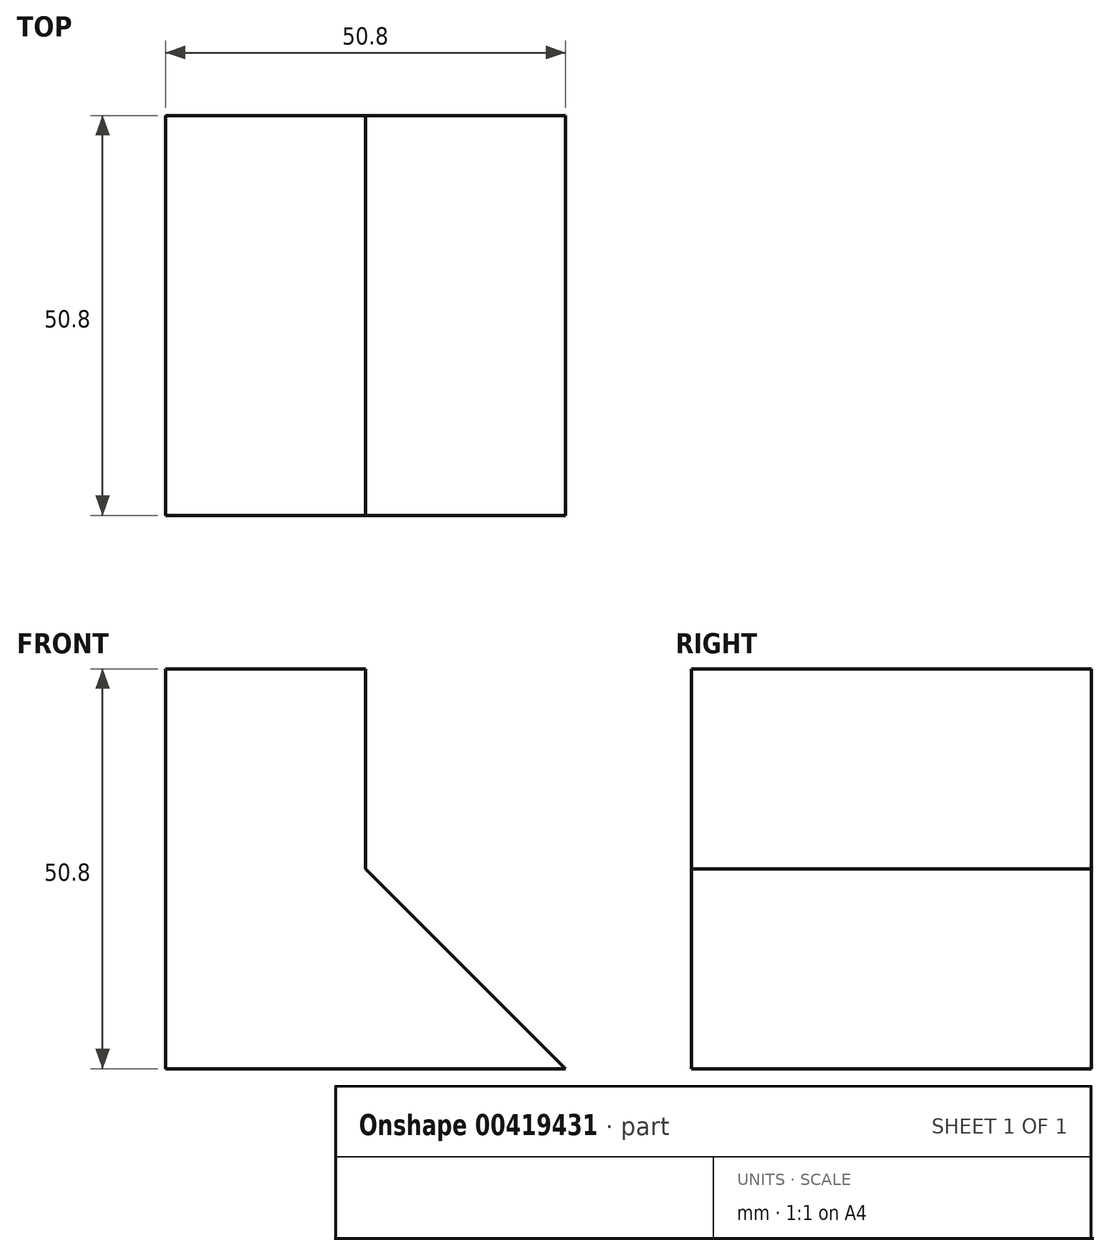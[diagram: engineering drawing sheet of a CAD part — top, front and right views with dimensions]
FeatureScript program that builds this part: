
annotation { "Feature Type Name" : "Feature", "Feature Type Description" : "" }
export const myFeature = defineFeature(function(context is Context, id is Id, definition is map)
    precondition{}
    {
        {
            var Q0;
            Q0=qCreatedBy(makeId("Front.planeOp"),FACE);
            var sketch = newSketch(context, id + "F0", { "sketchPlane" : qUnion([Q0])});
            skLineSegment(sketch, "E0", {"start": v(0, 0) * mm, "end": v(-50.8, 0) * mm});
            skLineSegment(sketch, "E1", {"start": v(-50.8, 0) * mm, "end": v(-50.8, 50.8) * mm});
            skLineSegment(sketch, "E2", {"start": v(-50.8, 50.8) * mm, "end": v(-25.4, 50.8) * mm});
            skLineSegment(sketch, "E3", {"start": v(-25.4, 50.8) * mm, "end": v(-25.4, 25.4) * mm});
            skLineSegment(sketch, "E4", {"start": v(-25.4, 25.4) * mm, "end": v(0, 0) * mm});
            skPoint(sketch, "E5.end.orphan", {"position": v(0, 25.4) * mm});
            skSolve(sketch);
        }
        {
            var Q0;
            Q0 = qSketchRegion(id + "F0", true);
            extrude(context, id + "F1", {"entities" : qUnion([Q0]), "depth" : 50.8 * mm});
        }
    });
